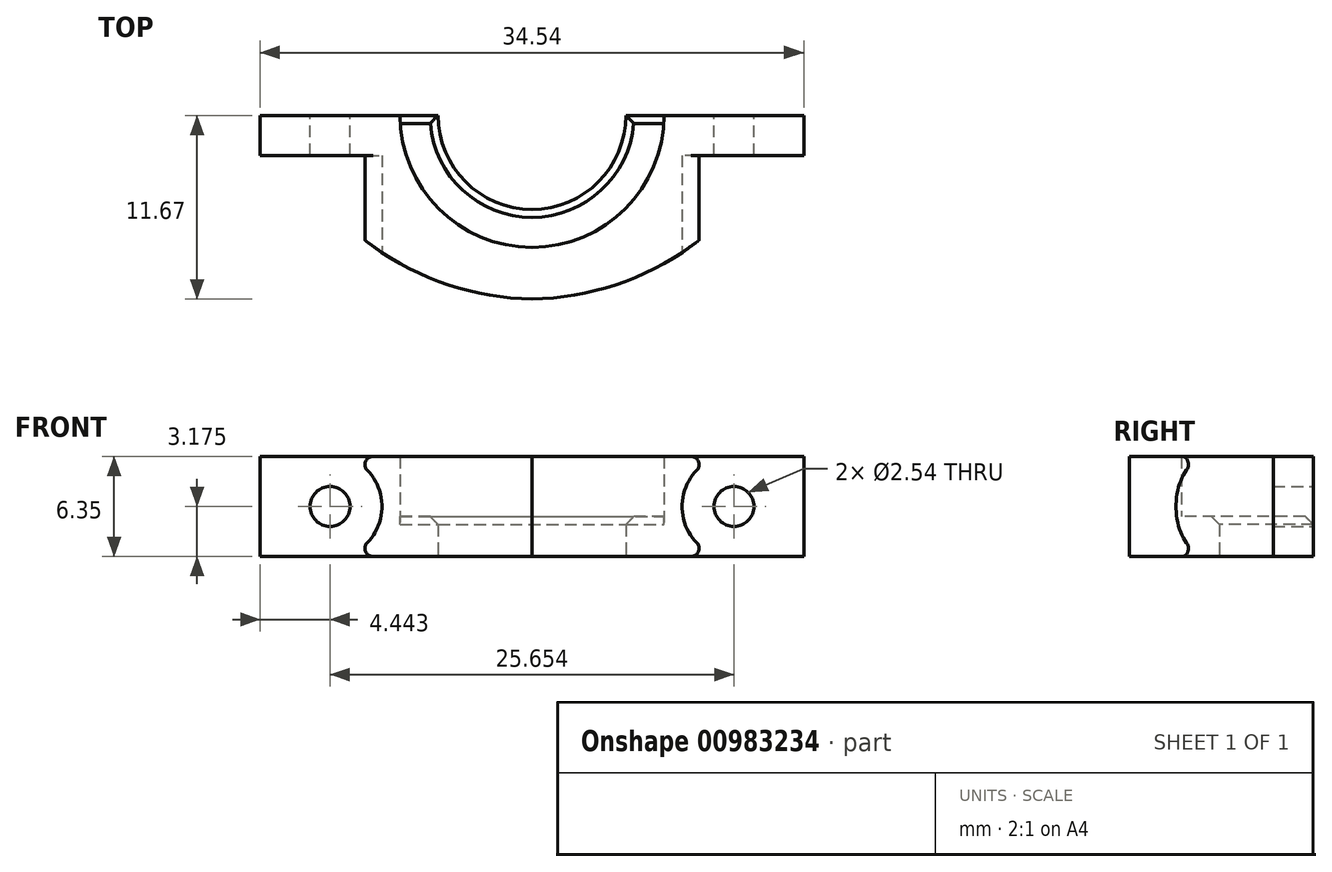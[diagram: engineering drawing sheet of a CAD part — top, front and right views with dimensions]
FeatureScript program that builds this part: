
annotation { "Feature Type Name" : "Feature", "Feature Type Description" : "" }
export const myFeature = defineFeature(function(context is Context, id is Id, definition is map)
    precondition{}
    {
        {
            var Q0;
            Q0=qCreatedBy(makeId("Top.planeOp"),FACE);
            var sketch = newSketch(context, id + "F0", { "sketchPlane" : qUnion([Q0])});
            skArc(sketch, "E0", {"start": v(-5.97, 0) * mm, "mid": v(0, -5.97) * mm, "end": v(5.97, 0) * mm});
            skArc(sketch, "E1", {"start": v(-8.38, 0) * mm, "mid": v(0, -8.38) * mm, "end": v(8.38, 0) * mm});
            skLineSegment(sketch, "E2", {"start": v(-8.38, 0) * mm, "end": v(-5.97, 0) * mm});
            skLineSegment(sketch, "E3", {"start": v(5.97, 0) * mm, "end": v(8.38, 0) * mm});
            skLineSegment(sketch, "E4", {"start": v(-8.38, 0) * mm, "end": v(-17.27, 0) * mm});
            skLineSegment(sketch, "E5", {"start": v(-17.27, 0) * mm, "end": v(-17.27, -2.54) * mm});
            skLineSegment(sketch, "E6", {"start": v(-17.27, -2.54) * mm, "end": v(-15.24, -2.54) * mm});
            skArc(sketch, "E7", {"start": v(-15.24, -2.54) * mm, "mid": v(-8.84, -9.14) * mm, "end": v(0, -11.67) * mm});
            skLineSegment(sketch, "E8", {"start": v(0, 13.12) * mm, "end": v(0, 11.52) * mm, "construction": true});
            skLineSegment(sketch, "E9.MirrorCS", {"start": v(8.38, 0) * mm, "end": v(17.27, 0) * mm});
            skLineSegment(sketch, "E10.MirrorCS", {"start": v(17.27, 0) * mm, "end": v(17.27, -2.54) * mm});
            skArc(sketch, "E11.MirrorCS", {"start": v(15.24, -2.54) * mm, "mid": v(8.84, -9.14) * mm, "end": v(0, -11.67) * mm});
            skLineSegment(sketch, "E12.MirrorCS", {"start": v(17.27, -2.54) * mm, "end": v(15.24, -2.54) * mm});
            skSolve(sketch);
        }
        {
            var Q0;
            Q0=makeQuery(id+"F0.imprint","IMPRINT",FACE,{"disambiguationData":[TD([[makeQuery(id+"F0.imprint","IMPRINT",EDGE,{"derivedFrom":sQuery(id+"F0.wireOp",EDGE,"E1")}),-1.0]])]});
            extrude(context, id + "F1", {"entities" : qUnion([Q0]), "depth" : 6.35 * mm, "offsetDistance" : 25.4 * mm});
        }
        {
            var Q0;
            Q0=makeQuery(id+"F0.imprint","IMPRINT",FACE,{"disambiguationData":[TD([[makeQuery(id+"F0.imprint","IMPRINT",EDGE,{"derivedFrom":sQuery(id+"F0.wireOp",EDGE,"E0")}),-1.0]])]});
            extrude(context, id + "F2", {"entities" : qUnion([Q0]), "operationType" : NewBodyOperationType.ADD, "depth" : 2.54 * mm, "offsetDistance" : 25.4 * mm});
        }
        {
            var Q0;
            Q0=makeQuery(id+"F2.boolean.opBoolean","MERGE",FACE,{"derivedFrom":[makeQuery(id+"F1.opExtrude","SWEPT_FACE",FACE,{"disambiguationData":[OSD([sQuery(id+"F0.wireOp",EDGE,"E9.MirrorCS")])]}),makeQuery(id+"F2.opExtrude","SWEPT_FACE",FACE,{"disambiguationData":[OSD([sQuery(id+"F0.wireOp",EDGE,"E3")])]})]});
            var sketch = newSketch(context, id + "F3", { "sketchPlane" : qUnion([Q0])});
            skCircle(sketch, "E13", {"center": v(-12.83, 3.18) * mm, "radius": 1.27 * mm});
            skCircle(sketch, "E14", {"center": v(12.83, 3.18) * mm, "radius": 1.27 * mm});
            skSolve(sketch);
        }
        {
            var Q0;
            Q0=makeQuery(id+"F3.imprint","IMPRINT",FACE,{"disambiguationData":[TD([[makeQuery(id+"F3.imprint","IMPRINT",EDGE,{"derivedFrom":sQuery(id+"F3.wireOp",EDGE,"E13")}),1.0]])]});
            var Q1;
            Q1=makeQuery(id+"F3.imprint","IMPRINT",FACE,{"disambiguationData":[TD([[makeQuery(id+"F3.imprint","IMPRINT",EDGE,{"derivedFrom":sQuery(id+"F3.wireOp",EDGE,"E14")}),1.0]])]});
            extrude(context, id + "F4", {"entities" : qUnion([Q0, Q1]), "operationType" : NewBodyOperationType.REMOVE, "oppositeDirection" : true, "depth" : 25.4 * mm, "offsetDistance" : 25.4 * mm});
        }
        {
            var Q0;
            Q0=makeQuery(id+"F2.boolean.opBoolean","MERGE",FACE,{"derivedFrom":[makeQuery(id+"F1.opExtrude","SWEPT_FACE",FACE,{"disambiguationData":[OSD([sQuery(id+"F0.wireOp",EDGE,"E4")])]}),makeQuery(id+"F2.opExtrude","SWEPT_FACE",FACE,{"disambiguationData":[OSD([sQuery(id+"F0.wireOp",EDGE,"E2")])]})]});
            cPlane(context, id + "F5", {"entities" : qUnion([Q0]), "cplaneType" : CPlaneType.OFFSET, "offset" : 12.7 * mm, "oppositeDirection" : true, "width" : 152.4 * mm, "height" : 152.4 * mm});
        }
        {
            var Q0;
            Q0=qCreatedBy(id+"F5.planeOp",FACE);
            var sketch = newSketch(context, id + "F6", { "sketchPlane" : qUnion([Q0])});
            skCircle(sketch, "E15", {"center": v(12.83, 3.18) * mm, "radius": 3.3 * mm});
            skCircle(sketch, "E16", {"center": v(-12.83, 3.18) * mm, "radius": 3.3 * mm});
            skLineSegment(sketch, "E17", {"start": v(20.64, 7.28) * mm, "end": v(20.64, -1.16) * mm});
            skLineSegment(sketch, "E18", {"start": v(20.64, -1.16) * mm, "end": v(12.73, -0.13) * mm});
            skLineSegment(sketch, "E19", {"start": v(20.64, 7.28) * mm, "end": v(12.9, 6.48) * mm});
            skLineSegment(sketch, "E20", {"start": v(-12.72, 6.48) * mm, "end": v(-20, 7.28) * mm});
            skLineSegment(sketch, "E21", {"start": v(-20, 7.28) * mm, "end": v(-20, -2) * mm});
            skLineSegment(sketch, "E22", {"start": v(-20, -2) * mm, "end": v(-12.78, -0.13) * mm});
            skSolve(sketch);
        }
        {
            var Q0;
            Q0=makeQuery(id+"F6.imprint","IMPRINT",FACE,{"disambiguationData":[TD([[makeQuery(id+"F6.imprint","IMPRINT",EDGE,{"derivedFrom":sQuery(id+"F6.wireOp",EDGE,"E15")}),1.0]])]});
            var Q1;
            Q1=makeQuery(id+"F6.imprint","IMPRINT",FACE,{"disambiguationData":[TD([[makeQuery(id+"F6.imprint","IMPRINT",EDGE,{"derivedFrom":sQuery(id+"F6.wireOp",EDGE,"E16")}),1.0]])]});
            var Q2;
            {var subQ0=sQuery(id+"F6.wireOp",EDGE,"E20");Q2=makeQuery(id+"F6.imprint","IMPRINT",FACE,{"disambiguationData":[TD([[makeQuery(id+"F6.imprint","IMPRINT",EDGE,{"derivedFrom":subQ0}),1.0]])]});}
            var Q3;
            Q3=makeQuery(id+"F6.imprint","IMPRINT",FACE,{"disambiguationData":[TD([[makeQuery(id+"F6.imprint","IMPRINT",EDGE,{"derivedFrom":sQuery(id+"F6.wireOp",EDGE,"E17")}),-1.0]])]});
            extrude(context, id + "F7", {"entities" : qUnion([Q0, Q1, Q2, Q3]), "operationType" : NewBodyOperationType.REMOVE, "depth" : 10.16 * mm, "offsetDistance" : 25.4 * mm});
        }
        {
            var Q0;
            Q0=makeQuery(id+"F7.boolean.opBoolean","INTERSECT",EDGE,{"derivedFrom":[makeQuery(id+"F1.opExtrude","CAP_FACE",FACE,{"disambiguationData":[OSD([sQuery(id+"F0.wireOp",EDGE,"E1"),sQuery(id+"F0.wireOp",EDGE,"E4"),sQuery(id+"F0.wireOp",EDGE,"E5"),sQuery(id+"F0.wireOp",EDGE,"E6"),sQuery(id+"F0.wireOp",EDGE,"E7"),sQuery(id+"F0.wireOp",EDGE,"E9.MirrorCS"),sQuery(id+"F0.wireOp",EDGE,"E10.MirrorCS"),sQuery(id+"F0.wireOp",EDGE,"E11.MirrorCS"),sQuery(id+"F0.wireOp",EDGE,"E12.MirrorCS")])],"isStart":false}),makeQuery(id+"F7.opExtrude","SWEPT_FACE",FACE,{"disambiguationData":[OSD([sQuery(id+"F6.wireOp",EDGE,"E15")])]})]});
            var Q1;
            {var subQ0=sQuery(id+"F0.wireOp",EDGE,"E1");Q1=makeQuery(id+"F7.boolean.opBoolean","INTERSECT",EDGE,{"derivedFrom":[makeQuery(id+"F2.boolean.opBoolean","MERGE",FACE,{"derivedFrom":[makeQuery(id+"F1.opExtrude","CAP_FACE",FACE,{"disambiguationData":[OSD([subQ0,sQuery(id+"F0.wireOp",EDGE,"E4"),sQuery(id+"F0.wireOp",EDGE,"E5"),sQuery(id+"F0.wireOp",EDGE,"E6"),sQuery(id+"F0.wireOp",EDGE,"E7"),sQuery(id+"F0.wireOp",EDGE,"E9.MirrorCS"),sQuery(id+"F0.wireOp",EDGE,"E10.MirrorCS"),sQuery(id+"F0.wireOp",EDGE,"E11.MirrorCS"),sQuery(id+"F0.wireOp",EDGE,"E12.MirrorCS")])],"isStart":true}),makeQuery(id+"F2.opExtrude","CAP_FACE",FACE,{"disambiguationData":[OSD([sQuery(id+"F0.wireOp",EDGE,"E0"),subQ0,sQuery(id+"F0.wireOp",EDGE,"E2"),sQuery(id+"F0.wireOp",EDGE,"E3")])],"isStart":true})]}),makeQuery(id+"F7.opExtrude","SWEPT_FACE",FACE,{"disambiguationData":[OSD([sQuery(id+"F6.wireOp",EDGE,"E15")])]})]});}
            var Q2;
            Q2=makeQuery(id+"F7.boolean.opBoolean","INTERSECT",EDGE,{"derivedFrom":[makeQuery(id+"F1.opExtrude","CAP_FACE",FACE,{"disambiguationData":[OSD([sQuery(id+"F0.wireOp",EDGE,"E1"),sQuery(id+"F0.wireOp",EDGE,"E4"),sQuery(id+"F0.wireOp",EDGE,"E5"),sQuery(id+"F0.wireOp",EDGE,"E6"),sQuery(id+"F0.wireOp",EDGE,"E7"),sQuery(id+"F0.wireOp",EDGE,"E9.MirrorCS"),sQuery(id+"F0.wireOp",EDGE,"E10.MirrorCS"),sQuery(id+"F0.wireOp",EDGE,"E11.MirrorCS"),sQuery(id+"F0.wireOp",EDGE,"E12.MirrorCS")])],"isStart":false}),makeQuery(id+"F7.opExtrude","SWEPT_FACE",FACE,{"disambiguationData":[OSD([sQuery(id+"F6.wireOp",EDGE,"E16")])]})]});
            var Q3;
            {var subQ0=sQuery(id+"F0.wireOp",EDGE,"E1");Q3=makeQuery(id+"F7.boolean.opBoolean","INTERSECT",EDGE,{"derivedFrom":[makeQuery(id+"F2.boolean.opBoolean","MERGE",FACE,{"derivedFrom":[makeQuery(id+"F1.opExtrude","CAP_FACE",FACE,{"disambiguationData":[OSD([subQ0,sQuery(id+"F0.wireOp",EDGE,"E4"),sQuery(id+"F0.wireOp",EDGE,"E5"),sQuery(id+"F0.wireOp",EDGE,"E6"),sQuery(id+"F0.wireOp",EDGE,"E7"),sQuery(id+"F0.wireOp",EDGE,"E9.MirrorCS"),sQuery(id+"F0.wireOp",EDGE,"E10.MirrorCS"),sQuery(id+"F0.wireOp",EDGE,"E11.MirrorCS"),sQuery(id+"F0.wireOp",EDGE,"E12.MirrorCS")])],"isStart":true}),makeQuery(id+"F2.opExtrude","CAP_FACE",FACE,{"disambiguationData":[OSD([sQuery(id+"F0.wireOp",EDGE,"E0"),subQ0,sQuery(id+"F0.wireOp",EDGE,"E2"),sQuery(id+"F0.wireOp",EDGE,"E3")])],"isStart":true})]}),makeQuery(id+"F7.opExtrude","SWEPT_FACE",FACE,{"disambiguationData":[OSD([sQuery(id+"F6.wireOp",EDGE,"E16")])]})]});}
            fillet(context, id + "F8", {"entities" : qUnion([Q0, Q1, Q2, Q3]), "radius" : 0.5 * mm, "tangentPropagation" : true, "allowEdgeOverflow" : false});
        }
        {
            var Q0;
            Q0=makeQuery(id+"F2.opExtrude","CAP_EDGE",EDGE,{"disambiguationData":[OSD([sQuery(id+"F0.wireOp",EDGE,"E0")])],"isStart":false});
            var Q1;
            Q1=makeQuery(id+"F2.opExtrude","CAP_EDGE",EDGE,{"disambiguationData":[OSD([sQuery(id+"F0.wireOp",EDGE,"E3")])],"isStart":false});
            var Q2;
            Q2=makeQuery(id+"F2.opExtrude","CAP_EDGE",EDGE,{"disambiguationData":[OSD([sQuery(id+"F0.wireOp",EDGE,"E2")])],"isStart":false});
            chamfer(context, id + "F9", {"entities" : qUnion([Q0, Q1, Q2]), "width" : 0.5 * mm, "tangentPropagation" : true});
        }
    });
